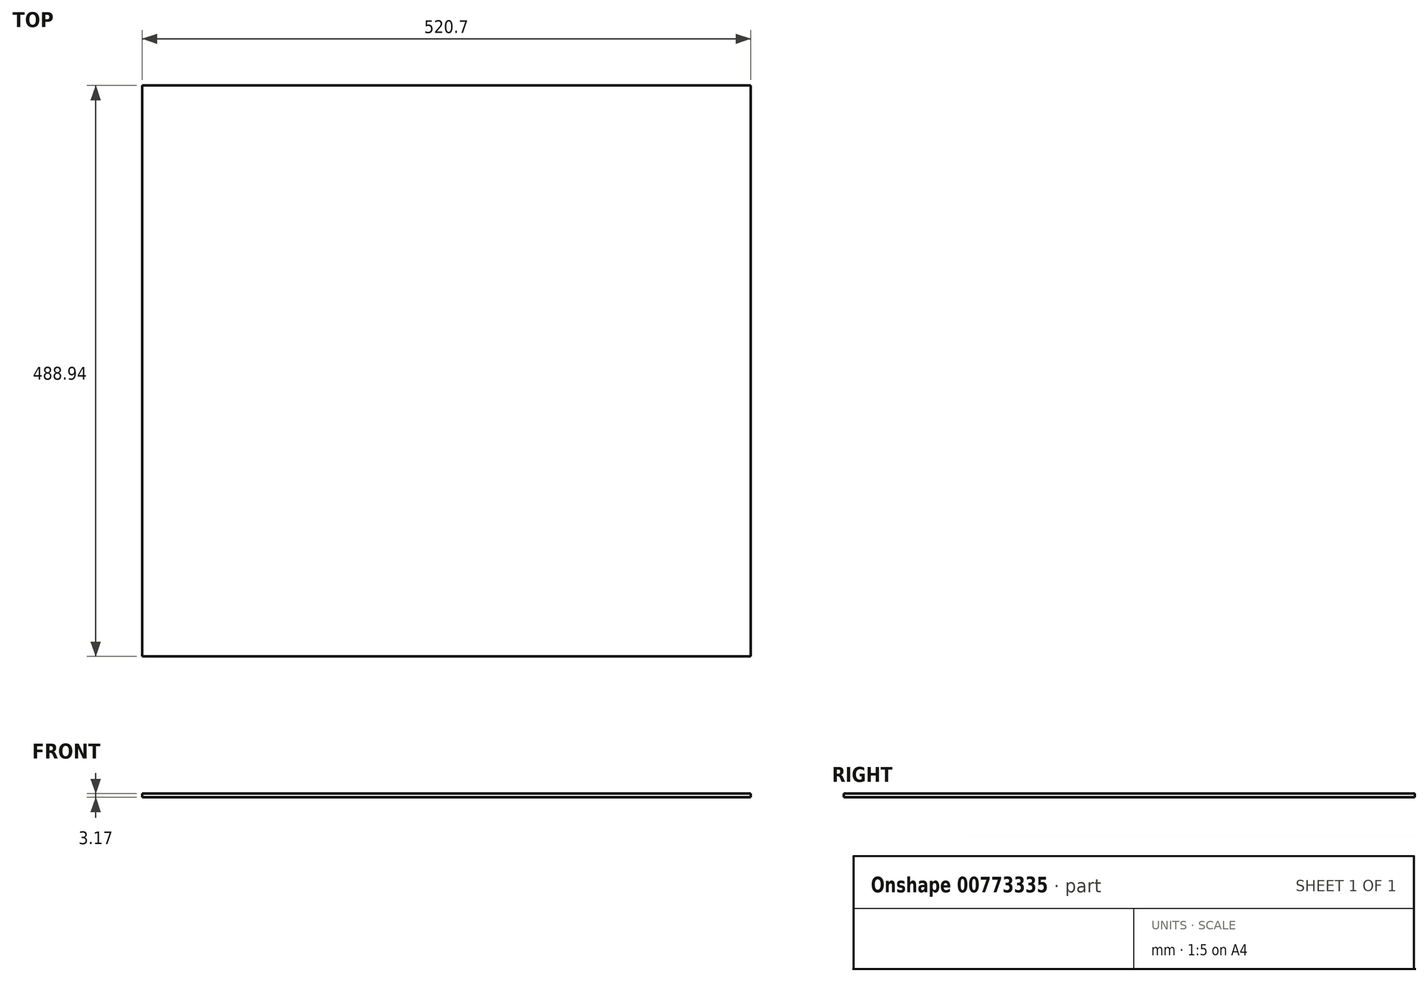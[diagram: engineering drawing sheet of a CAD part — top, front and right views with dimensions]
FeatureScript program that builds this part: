
annotation { "Feature Type Name" : "Feature", "Feature Type Description" : "" }
export const myFeature = defineFeature(function(context is Context, id is Id, definition is map)
    precondition{}
    {
        {
            var Q0;
            Q0=qCreatedBy(makeId("Top.planeOp"),FACE);
            var sketch = newSketch(context, id + "F0", { "sketchPlane" : qUnion([Q0])});
            skLineSegment(sketch, "E0.bottom", {"start": v(260.35, 244.48) * mm, "end": v(-260.35, 244.48) * mm});
            skLineSegment(sketch, "E0.top", {"start": v(260.35, -244.48) * mm, "end": v(-260.35, -244.48) * mm});
            skLineSegment(sketch, "E0.left", {"start": v(260.35, 244.48) * mm, "end": v(260.35, -244.48) * mm});
            skLineSegment(sketch, "E0.right", {"start": v(-260.35, 244.48) * mm, "end": v(-260.35, -244.48) * mm});
            skPoint(sketch, "E0.middle", {"position": v(0, 0) * mm});
            skSolve(sketch);
        }
        {
            var Q0;
            Q0 = qSketchRegion(id + "F0", true);
            extrude(context, id + "F1", {"entities" : qUnion([Q0]), "depth" : 3.17 * mm, "offsetDistance" : 25.4 * mm});
        }
    });
